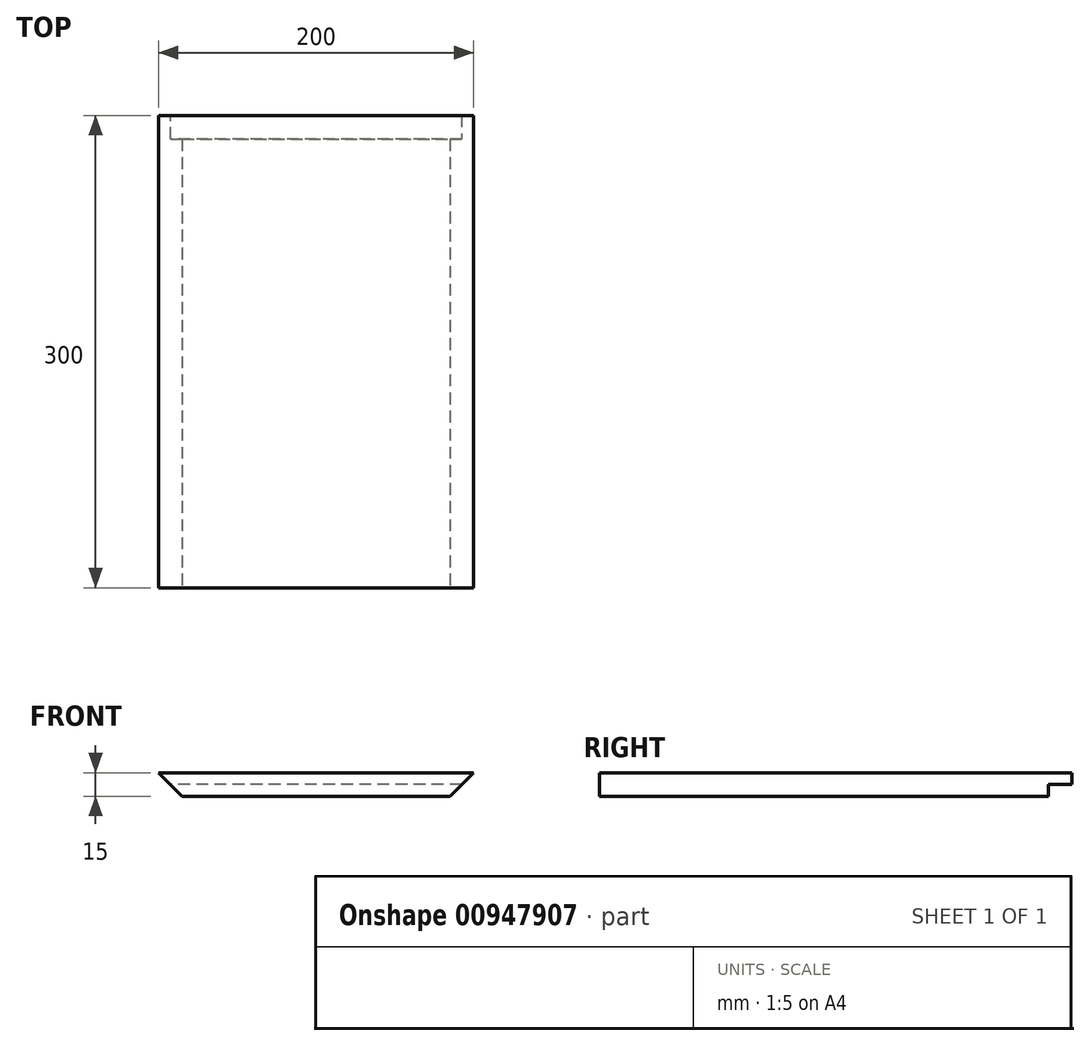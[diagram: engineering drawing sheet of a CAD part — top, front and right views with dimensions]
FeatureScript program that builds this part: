
annotation { "Feature Type Name" : "Feature", "Feature Type Description" : "" }
export const myFeature = defineFeature(function(context is Context, id is Id, definition is map)
    precondition{}
    {
        {
            var Q0;
            Q0=qCreatedBy(makeId("Right.planeOp"),FACE);
            cPlane(context, id + "F0", {"entities" : qUnion([Q0]), "cplaneType" : CPlaneType.OFFSET, "offset" : 100 * mm, "width" : 150 * mm, "height" : 150 * mm});
        }
        {
            var Q0;
            Q0=qCreatedBy(makeId("Right.planeOp"),FACE);
            cPlane(context, id + "F1", {"entities" : qUnion([Q0]), "cplaneType" : CPlaneType.OFFSET, "offset" : 100 * mm, "oppositeDirection" : true, "width" : 150 * mm, "height" : 150 * mm});
        }
        {
            var Q0;
            Q0=qCreatedBy(makeId("Front.planeOp"),FACE);
            cPlane(context, id + "F2", {"entities" : qUnion([Q0]), "cplaneType" : CPlaneType.OFFSET, "offset" : 150 * mm, "width" : 150 * mm, "height" : 150 * mm});
        }
        {
            var Q0;
            Q0=qCreatedBy(makeId("Front.planeOp"),FACE);
            cPlane(context, id + "F3", {"entities" : qUnion([Q0]), "cplaneType" : CPlaneType.OFFSET, "offset" : 150 * mm, "oppositeDirection" : true, "width" : 150 * mm, "height" : 150 * mm});
        }
        {
            var Q0;
            Q0=qCreatedBy(makeId("Top.planeOp"),FACE);
            cPlane(context, id + "F4", {"entities" : qUnion([Q0]), "cplaneType" : CPlaneType.OFFSET, "offset" : 300 * mm, "width" : 150 * mm, "height" : 150 * mm});
        }
        {
            var Q0;
            Q0=qCreatedBy(id+"F2.planeOp",FACE);
            var sketch = newSketch(context, id + "F5", { "sketchPlane" : qUnion([Q0])});
            skLineSegment(sketch, "E0", {"start": v(-100, 300) * mm, "end": v(100, 300) * mm});
            skLineSegment(sketch, "E1", {"start": v(100, 300) * mm, "end": v(85, 285) * mm});
            skLineSegment(sketch, "E2", {"start": v(85, 285) * mm, "end": v(-85, 285) * mm});
            skLineSegment(sketch, "E3", {"start": v(-85, 285) * mm, "end": v(-100, 300) * mm});
            skSolve(sketch);
        }
        {
            var Q0;
            Q0=makeQuery(id+"F5.imprint","IMPRINT",FACE,{"disambiguationData":[TD([[makeQuery(id+"F5.imprint","IMPRINT",EDGE,{"derivedFrom":sQuery(id+"F5.wireOp",EDGE,"E0")}),-1.0]])]});
            var Q1;
            Q1=qCreatedBy(id+"F3.planeOp",FACE);
            extrude(context, id + "F6", {"entities" : qUnion([Q0]), "endBound" : BoundingType.UP_TO_SURFACE, "oppositeDirection" : true, "depth" : 25 * mm, "endBoundEntityFace" : qUnion([Q1]), "offsetDistance" : 25 * mm});
        }
        {
            var Q0;
            Q0=qCreatedBy(id+"F3.planeOp",FACE);
            var sketch = newSketch(context, id + "F7", { "sketchPlane" : qUnion([Q0])});
            skLineSegment(sketch, "E4.bottom", {"start": v(100, 292.5) * mm, "end": v(-100, 292.5) * mm});
            skLineSegment(sketch, "E4.top", {"start": v(100, 280) * mm, "end": v(-100, 280) * mm});
            skLineSegment(sketch, "E4.left", {"start": v(100, 292.5) * mm, "end": v(100, 280) * mm});
            skLineSegment(sketch, "E4.right", {"start": v(-100, 292.5) * mm, "end": v(-100, 280) * mm});
            skSolve(sketch);
        }
        {
            var Q0;
            Q0 = qSketchRegion(id + "F7", true);
            extrude(context, id + "F8", {"entities" : qUnion([Q0]), "operationType" : NewBodyOperationType.REMOVE, "depth" : 15 * mm, "offsetDistance" : 25 * mm});
        }
    });
